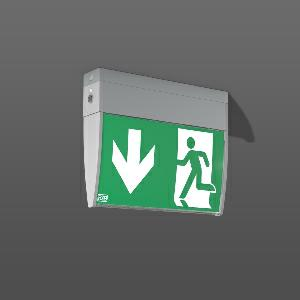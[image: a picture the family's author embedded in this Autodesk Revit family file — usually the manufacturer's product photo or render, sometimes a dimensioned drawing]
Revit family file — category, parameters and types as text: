
# Revit family: gsun_d_672219_004_1_04_e028
name_source: partatom
category: Lighting Fixtures
units: mm (PartAtom-declared; Revit-internal decimal feet)

## family parameters
Cut with Voids When Loaded = No
Host = Face
Light Source = No
Part Type = Normal
Room Calculation Point = No
Round Connector Dimension = Use Diameter
Shared = No

## types (1)
- GSUN D
    Apparent Load = 0 VA
    Default Elevation = 1800 mm
    Description = Series: GSUN D
Luminaire for escape route identification. Housing: extruded aluminium profile, powder-coated. 4 legends and 1 white lay in plastic sheet included. Universal mounting kit for ceiling and wall surface mounting. Electronic ballast included. Self-contained system with automatic self-test and feedback to the RZB monitoring system MULTIDIGIT. 
Colour: silver, matt (approx. RAL 9006)
Length: 247 mm
Width: 45 mm
Height: 200 mm
Weight: 0.9 kg
Operating mode: maintained power mode
Viewing Distance: 24 m
Duration time: 3 h
Lamp: LED
Socket: without socket
Colour temperature: 4000K
System power: 4.7 W
Control gear: Regulated power supply
Protection class: I
Type of protection: IP 30
    Height = 200 mm
    Lamp = 0 x
    Length = 247 mm
    Luminous efficacy = 0 lm/W
    Manufacturer = RZB
    ModVariant = No
    Model = 672219.004.1.04
    Mounting Place = Ceiling, Wall
    Mounting Type = Surface mounted
    Number of Poles = 1
    OnlyDefault = Yes
    Power Factor = 1
    Product Name = GSUN D
    Product group = Surface mounted ceiling and wall luminaires
    ProductGroupID = 305
    Protection Class = Protection class I
    Protection Degree = IP 30
    RLX_Detail_Level = 1
    RLX_Emergency_Light_Flux = 0 lm
    RLX_Emergency_Type = 0
    RLX_Emergency_Type_DB = No
    RlxData = <blob elided: 30365 chars, md5=43c93fdd>
    Standby Power = 0 W
    System Light Flux = 0 lm
    System Power = 0 W
    Type Comments = Product without accessories
    Type Image = 671995.004.1.jpg
    URL = http://relux.com
    VarID = ---
    Voltage = 230 V
    Voltage Range = 220-240 V
    Weight = 0.00 kg
    Width = 45 mm

## geometry (parser evidence)
native form markers: Blend x4, Sweep x10
no freeform markers — native parametric forms only
